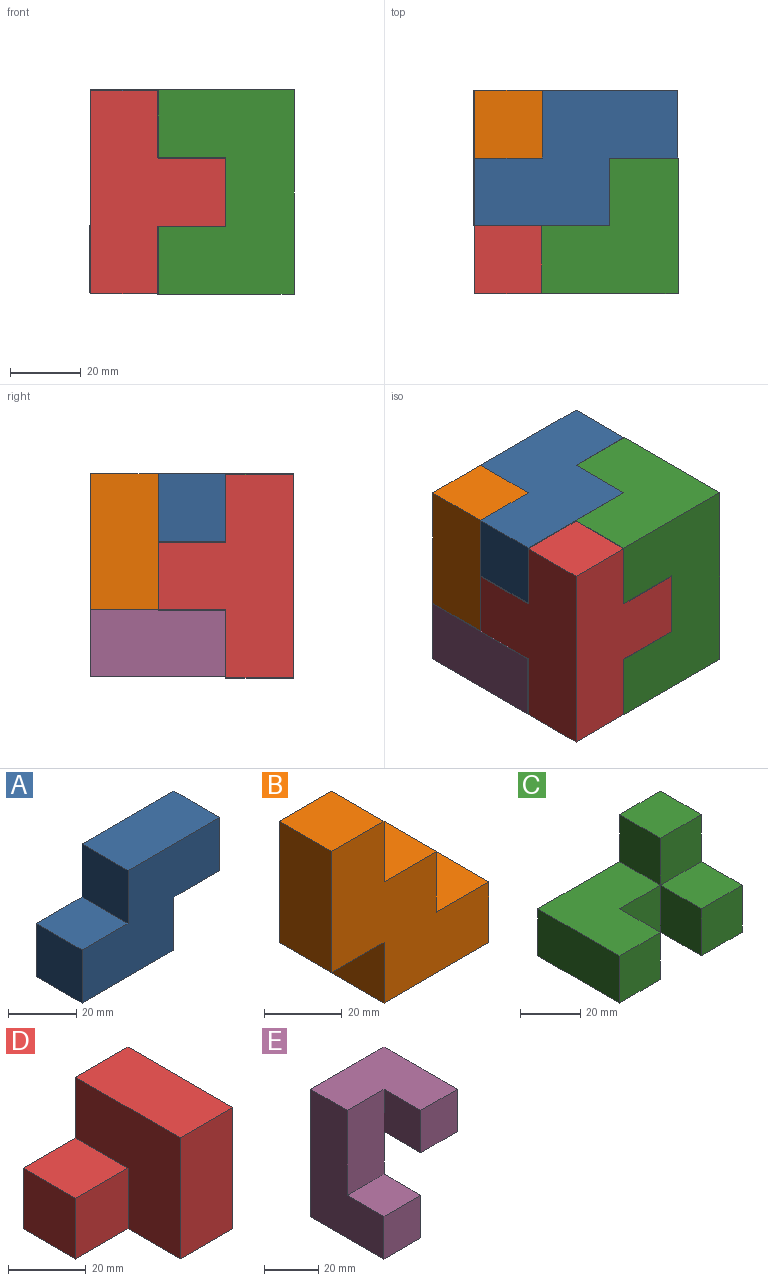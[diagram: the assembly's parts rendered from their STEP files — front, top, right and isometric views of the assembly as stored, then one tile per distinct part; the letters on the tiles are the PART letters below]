
ASSEMBLY  parts=5 mates=4
PART A: 10 faces, bbox 57.2x19.1x38.1 mm
  f0: plane 38.1x19.05mm, normal (0,0,-1), area 725.8mm2, adj f1,f7,f8,f9
  f1: plane 19.05x19.05mm, normal (1,0,0), area 362.9mm2, adj f0,f2,f8,f9
  f2: plane 19.05x19.05mm, normal (0,0,-1), area 362.9mm2, adj f1,f3,f8,f9
  f3: plane 19.05x19.05mm, normal (1,0,0), area 362.9mm2, adj f2,f4,f8,f9
  f4: plane 38.1x19.05mm, normal (0,0,1), area 725.8mm2, adj f3,f5,f8,f9
  f5: plane 19.05x19.05mm, normal (-1,0,0), area 362.9mm2, adj f4,f6,f8,f9
  f6: plane 19.05x19.05mm, normal (0,0,1), area 362.9mm2, adj f5,f7,f8,f9
  f7: plane 19.05x19.05mm, normal (-1,0,0), area 362.9mm2, adj f0,f6,f8,f9
  f8: plane 57.15x38.1mm, normal (0,-1,0), area 1451.6mm2, adj f0,f1,f2,f3,f4,f5,f6,f7
  f9: plane 57.15x38.1mm, normal (0,1,0), area 1451.6mm2, adj f0,f1,f2,f3,f4,f5,f6,f7
PART B: 12 faces, bbox 57.2x19.1x57.2 mm
  f0: plane 19.05x19.05mm, normal (0,0,1), area 362.9mm2, adj f1,f9,f10,f11
  f1: plane 19.05x19.05mm, normal (1,0,0), area 362.9mm2, adj f0,f2,f10,f11
  f2: plane 19.05x19.05mm, normal (0,0,1), area 362.9mm2, adj f1,f3,f10,f11
  f3: plane 19.05x19.05mm, normal (1,0,0), area 362.9mm2, adj f2,f4,f10,f11
  f4: plane 19.05x19.05mm, normal (0,0,1), area 362.9mm2, adj f3,f5,f10,f11
  f5: plane 38.1x19.05mm, normal (-1,0,0), area 725.8mm2, adj f4,f6,f10,f11
  f6: plane 19.05x19.05mm, normal (0,0,-1), area 362.9mm2, adj f5,f7,f10,f11
  f7: plane 19.05x19.05mm, normal (-1,0,0), area 362.9mm2, adj f6,f8,f10,f11
  f8: plane 38.1x19.05mm, normal (0,0,-1), area 725.8mm2, adj f7,f9,f10,f11
  f9: plane 19.05x19.05mm, normal (1,0,0), area 362.9mm2, adj f0,f8,f10,f11
  f10: plane 57.15x57.15mm, normal (0,-1,0), area 1814.5mm2, adj f0,f1,f2,f3,f4,f5,f6,f7
  f11: plane 57.15x57.15mm, normal (0,1,0), area 1814.5mm2, adj f0,f1,f2,f3,f4,f5,f6,f7
PART C: 14 faces, bbox 57.5x38.3x38.1 mm
  f0: plane 19.17x19.17mm, normal (0,0,1), area 367.5mm2, adj f5,f6,f7,f11
  f1: plane 38.34x19.05mm, normal (-1,0,0), area 730.4mm2, adj f2,f8,f9,f10
  f2: plane 19.17x19.05mm, normal (0,-1,0), area 365.2mm2, adj f1,f3,f9,f10
  f3: plane 19.17x19.05mm, normal (1,0,0), area 365.2mm2, adj f2,f4,f9,f10
  f4: plane 19.17x19.05mm, normal (0,-1,0), area 365.2mm2, adj f3,f5,f9,f10
  f5: plane 19.17x19.05mm, normal (-1,0,0), area 365.2mm2, adj f0,f4,f6,f10
  f6: plane 19.17x19.05mm, normal (0,-1,0), area 365.2mm2, adj f0,f5,f7,f10
  f7: plane 38.34x38.1mm, normal (1,0,0), area 1095.6mm2, adj f0,f6,f8,f10,f11,f13
  f8: plane 57.51x38.1mm, normal (0,1,0), area 1460.8mm2, adj f1,f7,f9,f10,f12,f13
  f9: plane 38.34x38.34mm, normal (0,0,1), area 1102.5mm2, adj f1,f2,f3,f4,f8,f12
  f10: plane 57.51x38.34mm, normal (0,0,-1), area 1837.5mm2, adj f1,f2,f3,f4,f5,f6,f7,f8
  f11: plane 19.17x19.05mm, normal (0,-1,0), area 365.2mm2, adj f0,f7,f12,f13
  f12: plane 19.17x19.05mm, normal (-1,0,0), area 365.2mm2, adj f8,f9,f11,f13
  f13: plane 19.17x19.17mm, normal (0,0,1), area 367.5mm2, adj f7,f8,f11,f12
PART D: 12 faces, bbox 57.2x38.1x38.1 mm
  f0: plane 19.05x19.05mm, normal (0,-1,0), area 362.9mm2, adj f2,f3,f4,f5
  f1: plane 19.05x19.05mm, normal (-1,0,0), area 362.9mm2, adj f2,f8,f9,f10
  f2: plane 57.15x38.1mm, normal (0,0,-1), area 1451.6mm2, adj f0,f1,f3,f5,f7,f9,f10,f11
  f3: plane 19.05x19.05mm, normal (1,0,0), area 362.9mm2, adj f0,f2,f4,f10
  f4: plane 19.05x19.05mm, normal (0,0,1), area 362.9mm2, adj f0,f3,f5,f10
  f5: plane 38.1x38.1mm, normal (1,0,0), area 1088.7mm2, adj f0,f2,f4,f6,f10,f11
  f6: plane 38.1x19.05mm, normal (0,0,1), area 725.8mm2, adj f5,f7,f10,f11
  f7: plane 38.1x38.1mm, normal (-1,0,0), area 1088.7mm2, adj f2,f6,f8,f9,f10,f11
  f8: plane 19.05x19.05mm, normal (0,0,1), area 362.9mm2, adj f1,f7,f9,f10
  f9: plane 19.05x19.05mm, normal (0,-1,0), area 362.9mm2, adj f1,f2,f7,f8
  f10: plane 57.15x38.1mm, normal (0,1,0), area 1451.6mm2, adj f1,f2,f3,f4,f5,f6,f7,f8
  f11: plane 38.1x19.05mm, normal (0,-1,0), area 725.8mm2, adj f2,f5,f6,f7
PART E: 12 faces, bbox 38.1x38.1x57.4 mm
  f0: plane 38.3x38.1mm, normal (1,0,0), area 1094.4mm2, adj f1,f5,f6,f7,f10,f11
  f1: plane 38.1x19.05mm, normal (0,0,-1), area 725.8mm2, adj f0,f2,f7,f8,f9
  f2: plane 38.1x19.05mm, normal (1,0,0), area 725.8mm2, adj f1,f3,f7,f9
  f3: plane 38.1x38.1mm, normal (0,0,1), area 1088.7mm2, adj f2,f4,f6,f7,f8,f9
  f4: plane 57.35x38.1mm, normal (-1,0,0), area 1457.3mm2, adj f3,f5,f6,f7,f10,f11
  f5: plane 38.1x19.05mm, normal (0,0,-1), area 725.8mm2, adj f0,f4,f7,f11
  f6: plane 38.2x19.05mm, normal (0,-1,0), area 727.7mm2, adj f0,f3,f4,f8,f10
  f7: plane 57.35x38.1mm, normal (0,1,0), area 1455.4mm2, adj f0,f1,f2,f3,f4,f5
  f8: plane 19.05x19.05mm, normal (-1,0,0), area 362.9mm2, adj f1,f3,f6,f9
  f9: plane 19.05x19.05mm, normal (0,-1,0), area 362.9mm2, adj f1,f2,f3,f8
  f10: plane 19.05x19.05mm, normal (0,0,1), area 362.9mm2, adj f0,f4,f6,f11
  f11: plane 19.15x19.05mm, normal (0,-1,0), area 364.8mm2, adj f0,f4,f5,f10
PLACE A rot(axis=(-1,0,0),90deg) t=(-92.01,23.28,-125.64)mm
PLACE B t=(-85.8,61.38,-163.74)mm
PLACE C rot(axis=(-0.58,-0.58,-0.58),120deg) t=(-73.08,4.23,-164.1)mm
PLACE D rot(axis=(-0.71,0,-0.71),180deg) t=(-92.01,4.23,-163.98)mm
PLACE E rot(axis=(0.71,0,0.71),180deg) t=(-92.21,23.28,-163.74)mm
MATE fastened C.f11 <-> A.f1  axis (-1,0,0) through (-53.91,23.28,-106.59)mm
MATE fastened A.f6 <-> B.f10  axis (0,1,0) through (-92.01,42.33,-106.59)mm
MATE fastened C.f4 <-> D.f6  axis (-1,0,0) through (-53.91,4.23,-144.93)mm
MATE fastened E.f2 <-> A.f9  axis (0,0,1) through (-34.86,61.38,-125.64)mm
